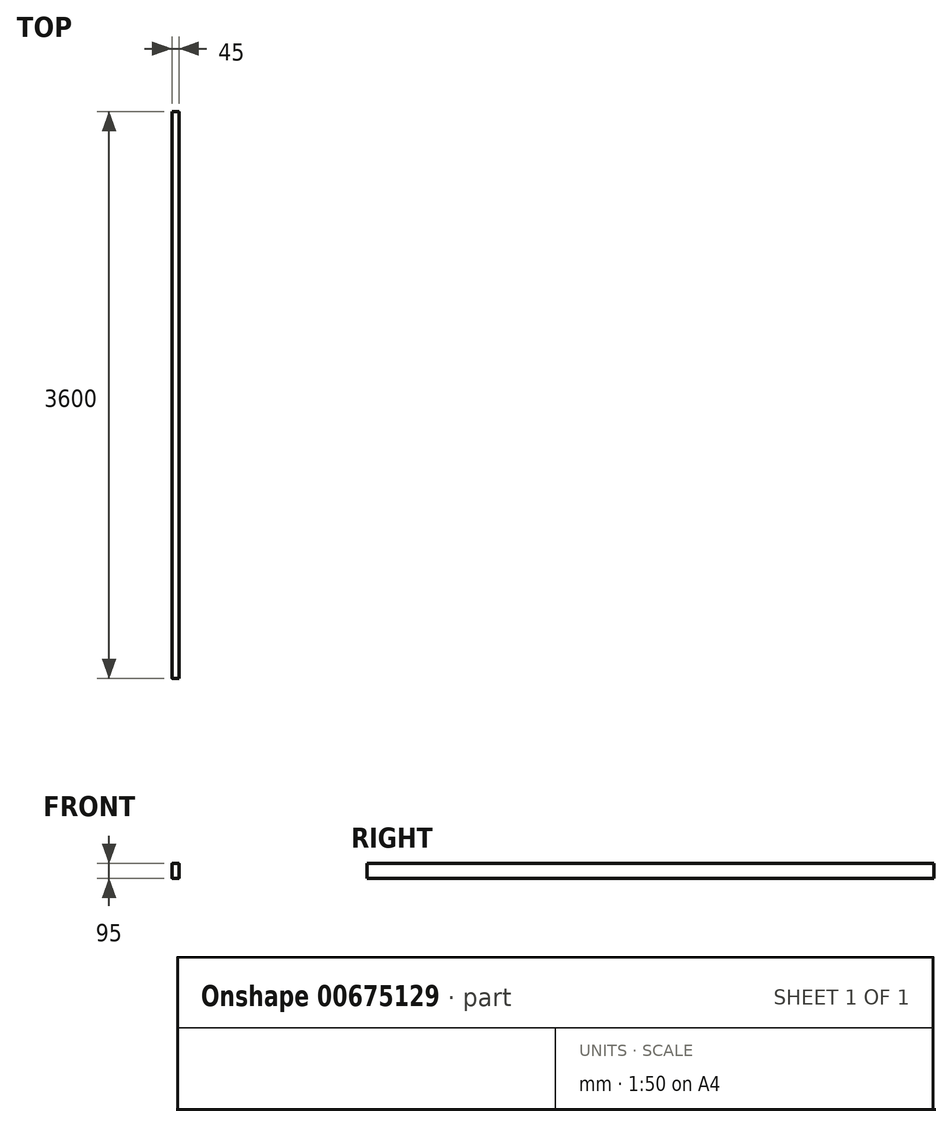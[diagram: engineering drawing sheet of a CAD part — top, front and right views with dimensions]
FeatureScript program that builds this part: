
annotation { "Feature Type Name" : "Feature", "Feature Type Description" : "" }
export const myFeature = defineFeature(function(context is Context, id is Id, definition is map)
    precondition{}
    {
        {
            var Q0;
            Q0=qCreatedBy(makeId("Front.planeOp"),FACE);
            var sketch = newSketch(context, id + "F0", { "sketchPlane" : qUnion([Q0])});
            skLineSegment(sketch, "E0.bottom", {"start": v(3, 0) * mm, "end": v(42, 0) * mm});
            skLineSegment(sketch, "E0.top", {"start": v(3, 95) * mm, "end": v(42, 95) * mm});
            skLineSegment(sketch, "E0.left", {"start": v(0, 3) * mm, "end": v(0, 92) * mm});
            skLineSegment(sketch, "E0.right", {"start": v(45, 3) * mm, "end": v(45, 92) * mm});
            skPoint(sketch, "E1.visualSharp", {"position": v(0, 95) * mm});
            skArc(sketch, "E1.filletArc", {"start": v(3, 95) * mm, "mid": v(0.88, 94.12) * mm, "end": v(0, 92) * mm});
            skPoint(sketch, "E2.visualSharp", {"position": v(45, 95) * mm});
            skArc(sketch, "E2.filletArc", {"start": v(45, 92) * mm, "mid": v(44.12, 94.12) * mm, "end": v(42, 95) * mm});
            skPoint(sketch, "E3.visualSharp", {"position": v(45, 0) * mm});
            skArc(sketch, "E3.filletArc", {"start": v(42, 0) * mm, "mid": v(44.12, 0.88) * mm, "end": v(45, 3) * mm});
            skPoint(sketch, "E4.visualSharp", {"position": v(0, 0) * mm});
            skArc(sketch, "E4.filletArc", {"start": v(0, 3) * mm, "mid": v(0.88, 0.88) * mm, "end": v(3, 0) * mm});
            skSolve(sketch);
        }
        {
            var Q0;
            Q0 = qSketchRegion(id + "F0", true);
            extrude(context, id + "F1", {"entities" : qUnion([Q0]), "depth" : 3600 * mm, "offsetDistance" : 25 * mm});
        }
    });
